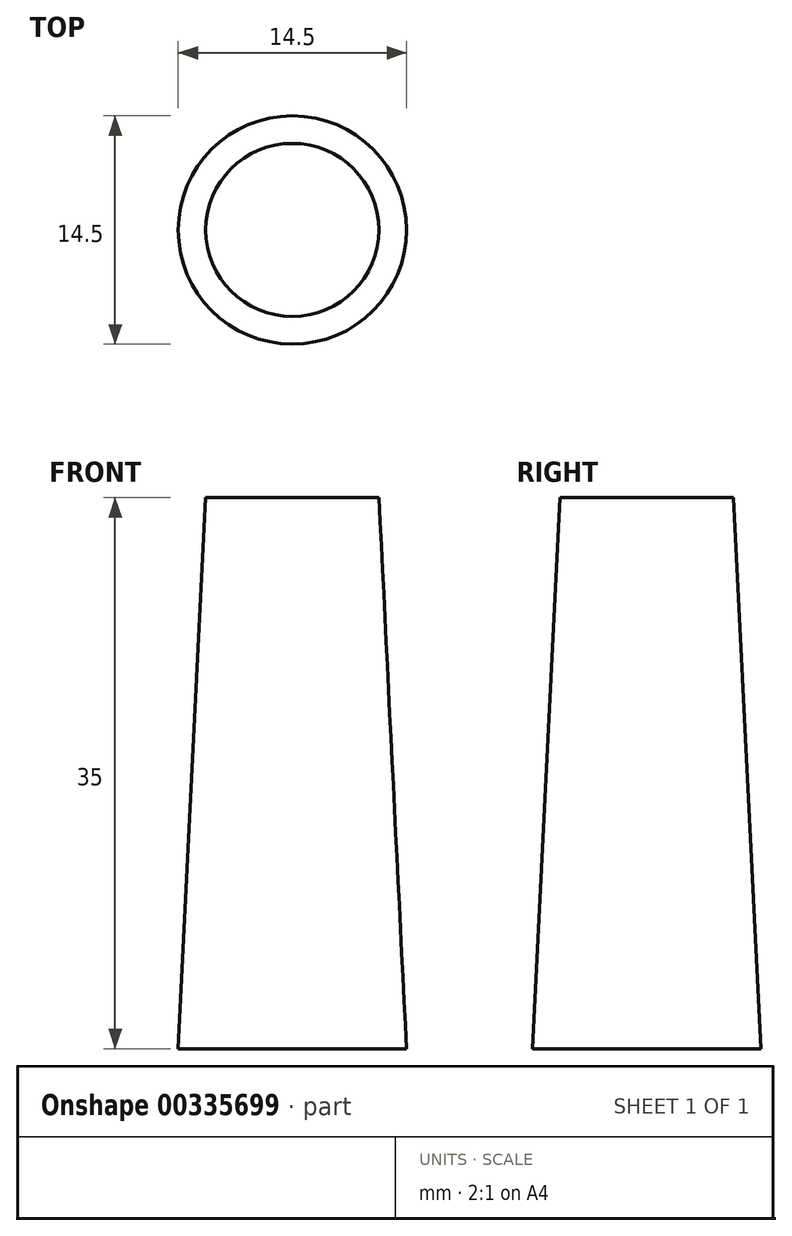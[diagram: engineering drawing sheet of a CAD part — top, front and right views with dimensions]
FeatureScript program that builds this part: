
annotation { "Feature Type Name" : "Feature", "Feature Type Description" : "" }
export const myFeature = defineFeature(function(context is Context, id is Id, definition is map)
    precondition{}
    {
        {
            var Q0;
            Q0=qCreatedBy(makeId("Top.planeOp"),FACE);
            cPlane(context, id + "F0", {"entities" : qUnion([Q0]), "cplaneType" : CPlaneType.OFFSET, "offset" : 35 * mm, "width" : 150 * mm, "height" : 150 * mm});
        }
        {
            var Q0;
            Q0=qCreatedBy(makeId("Top.planeOp"),FACE);
            var sketch = newSketch(context, id + "F1", { "sketchPlane" : qUnion([Q0])});
            skCircle(sketch, "E0", {"center": v(0, 0) * mm, "radius": 7.25 * mm});
            skSolve(sketch);
        }
        {
            var Q0;
            Q0=qCreatedBy(id+"F0.planeOp",FACE);
            var sketch = newSketch(context, id + "F2", { "sketchPlane" : qUnion([Q0])});
            skPoint(sketch, "E1.0", {"position": v(0, 0) * mm});
            skCircle(sketch, "E2", {"center": v(0, 0) * mm, "radius": 5.5 * mm});
            skSolve(sketch);
        }
        {
            var Q0;
            Q0=makeQuery(id+"F2.imprint","IMPRINT",FACE,{"disambiguationData":[TD([[makeQuery(id+"F2.imprint","IMPRINT",EDGE,{"derivedFrom":sQuery(id+"F2.wireOp",EDGE,"E2")}),1.0]])]});
            var Q1;
            Q1=makeQuery(id+"F1.imprint","IMPRINT",FACE,{"disambiguationData":[TD([[makeQuery(id+"F1.imprint","IMPRINT",EDGE,{"derivedFrom":sQuery(id+"F1.wireOp",EDGE,"E0")}),1.0]])]});
            loft(context, id + "F3", {"sheetProfilesArray" : [{ "sheetProfileEntities" : qUnion([Q0]) }, { "sheetProfileEntities" : qUnion([Q1]) }]});
        }
    });
